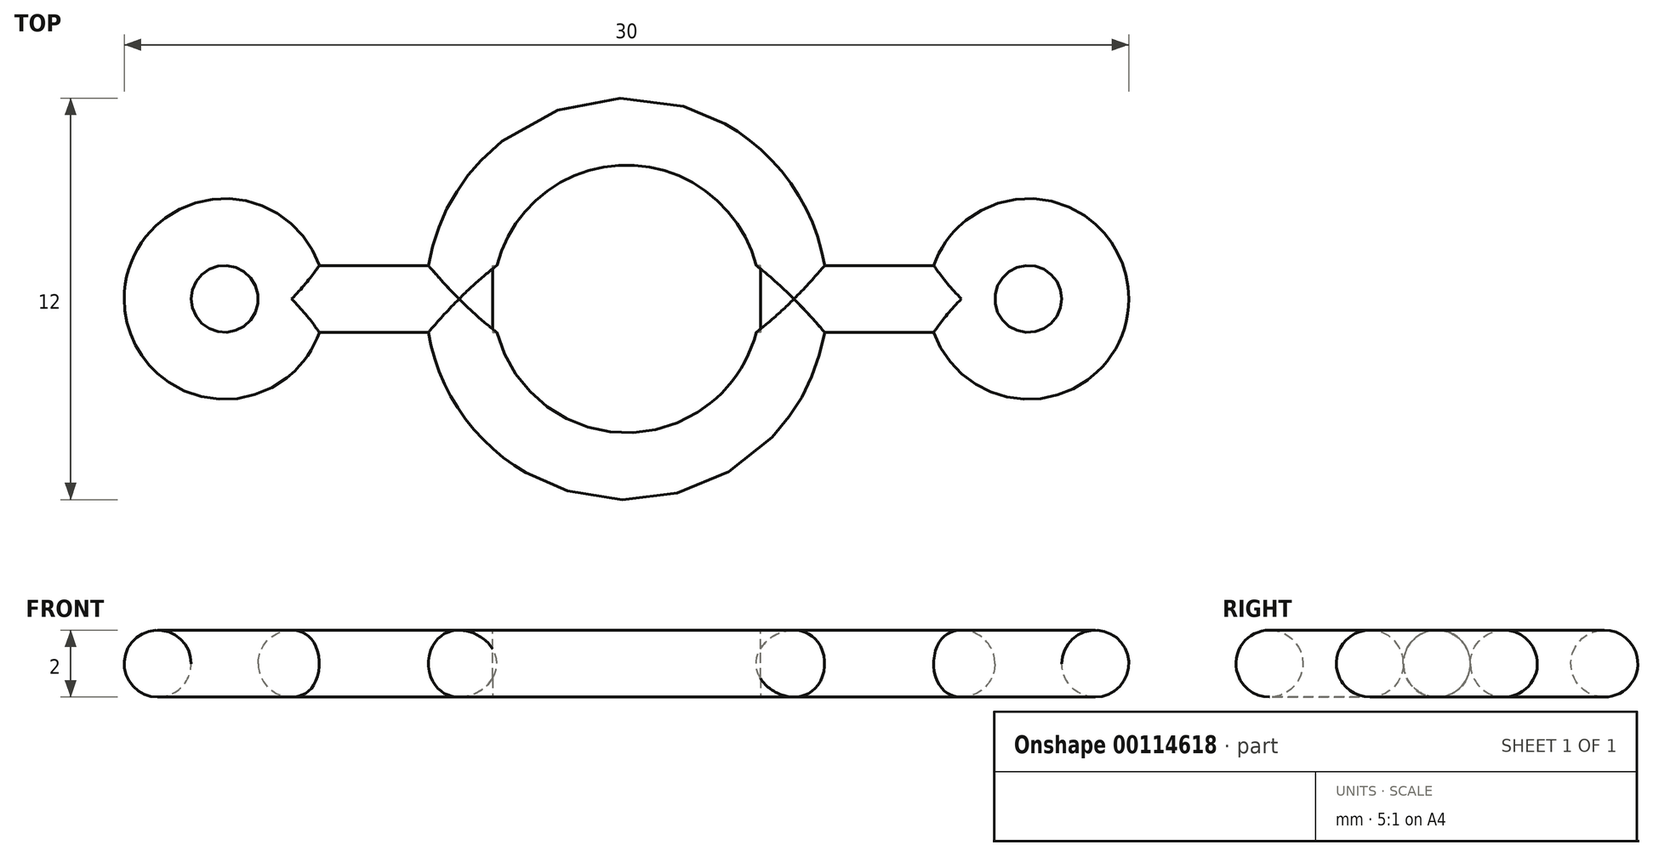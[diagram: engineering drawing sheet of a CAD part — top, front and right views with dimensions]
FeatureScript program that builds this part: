
annotation { "Feature Type Name" : "Feature", "Feature Type Description" : "" }
export const myFeature = defineFeature(function(context is Context, id is Id, definition is map)
    precondition{}
    {
        {
            var Q0;
            Q0=qCreatedBy(makeId("Front.planeOp"),FACE);
            var sketch = newSketch(context, id + "F0", { "sketchPlane" : qUnion([Q0])});
            skCircle(sketch, "E0", {"center": v(0, 0) * mm, "radius": 4 * mm, "construction": true});
            skLineSegment(sketch, "E1", {"start": v(4, 0) * mm, "end": v(6, 0) * mm});
            skCircle(sketch, "E2", {"center": v(5, 0) * mm, "radius": 1 * mm});
            skLineSegment(sketch, "E3", {"start": v(6, 0) * mm, "end": v(12, 0) * mm, "construction": true});
            skLineSegment(sketch, "E4", {"start": v(12, 0) * mm, "end": v(14, 0) * mm, "construction": true});
            skCircle(sketch, "E5", {"center": v(14, 0) * mm, "radius": 1 * mm});
            skSolve(sketch);
        }
        {
            var Q0;
            Q0=qCreatedBy(makeId("Top.planeOp"),FACE);
            var sketch = newSketch(context, id + "F1", { "sketchPlane" : qUnion([Q0])});
            skCircle(sketch, "E6", {"center": v(0, 0) * mm, "radius": 5 * mm, "construction": true});
            skLineSegment(sketch, "E7", {"start": v(5, 0) * mm, "end": v(12, 0) * mm, "construction": true});
            skCircle(sketch, "E8", {"center": v(12, 0) * mm, "radius": 2 * mm, "construction": true});
            skLineSegment(sketch, "E9", {"start": v(0, 0) * mm, "end": v(0, 15) * mm, "construction": true});
            skLineSegment(sketch, "E10", {"start": v(0, 0) * mm, "end": v(0, -15) * mm});
            skSolve(sketch);
        }
        {
            var Q0;
            {var subQ0=sQuery(id+"F0.wireOp",EDGE,"E1");Q0=makeQuery(id+"F0.imprint","IMPRINT",FACE,{"disambiguationData":[TD([[makeQuery(id+"F0.imprint","IMPRINT",EDGE,{"derivedFrom":subQ0}),1.0]])]});}
            var Q1;
            {var subQ0=sQuery(id+"F0.wireOp",EDGE,"E1");Q1=makeQuery(id+"F0.imprint","IMPRINT",FACE,{"disambiguationData":[TD([[makeQuery(id+"F0.imprint","IMPRINT",EDGE,{"derivedFrom":subQ0}),-1.0]])]});}
            var Q2;
            Q2=sQuery(id+"F1.wireOp",EDGE,"E6");
            revolve(context, id + "F2", {"entities" : qUnion([Q0, Q1]), "axis" : qUnion([Q2]), "revolveType" : RevolveType.SYMMETRIC, "angle" : 180 * degree});
        }
        {
            var Q0;
            Q0=makeQuery(id+"F0.imprint","IMPRINT",FACE,{"disambiguationData":[TD([[makeQuery(id+"F0.imprint","IMPRINT",EDGE,{"derivedFrom":sQuery(id+"F0.wireOp",EDGE,"E5")}),1.0]])]});
            var Q1;
            Q1=sQuery(id+"F1.wireOp",EDGE,"E8");
            revolve(context, id + "F3", {"entities" : qUnion([Q0]), "axis" : qUnion([Q1]), "revolveType" : RevolveType.FULL});
        }
        {
            var Q0;
            Q0=qCreatedBy(makeId("Right.planeOp"),FACE);
            var sketch = newSketch(context, id + "F4", { "sketchPlane" : qUnion([Q0])});
            skCircle(sketch, "E11", {"center": v(0, 0) * mm, "radius": 1 * mm});
            skSolve(sketch);
        }
        {
            var Q0;
            Q0=makeQuery(id+"F4.imprint","IMPRINT",FACE,{"disambiguationData":[TD([[makeQuery(id+"F4.imprint","IMPRINT",EDGE,{"derivedFrom":sQuery(id+"F4.wireOp",EDGE,"E11")}),1.0]])]});
            extrude(context, id + "F5", {"entities" : qUnion([Q0]), "depth" : 10 * mm});
        }
        {
            var Q0;
            Q0=makeQuery(id+"F5.opExtrude","CAP_FACE",FACE,{"disambiguationData":[OSD([sQuery(id+"F4.wireOp",EDGE,"E11")])],"isStart":true});
            extrude(context, id + "F6", {"entities" : qUnion([Q0]), "operationType" : NewBodyOperationType.REMOVE, "oppositeDirection" : true, "depth" : 4 * mm});
        }
        {
            var Q0;
            Q0=makeQuery(id+"F3.opRevolve","SWEPT_BODY",BODY,{"disambiguationData":[OSD([sQuery(id+"F0.wireOp",EDGE,"E5")])]});
            var Q1;
            Q1=makeQuery(id+"F2.opRevolve","SWEPT_BODY",BODY,{"disambiguationData":[OSD([sQuery(id+"F0.wireOp",EDGE,"E2")])]});
            var Q2;
            Q2=makeQuery(id+"F5.opExtrude","SWEPT_BODY",BODY,{"disambiguationData":[OSD([sQuery(id+"F4.wireOp",EDGE,"E11")])]});
            var Q3;
            Q3=qCreatedBy(makeId("Right.planeOp"),FACE);
            mirror(context, id + "F7", {"operationType" : NewBodyOperationType.ADD, "entities" : qUnion([Q0, Q1, Q2]), "mirrorPlane" : qUnion([Q3])});
        }
    });
